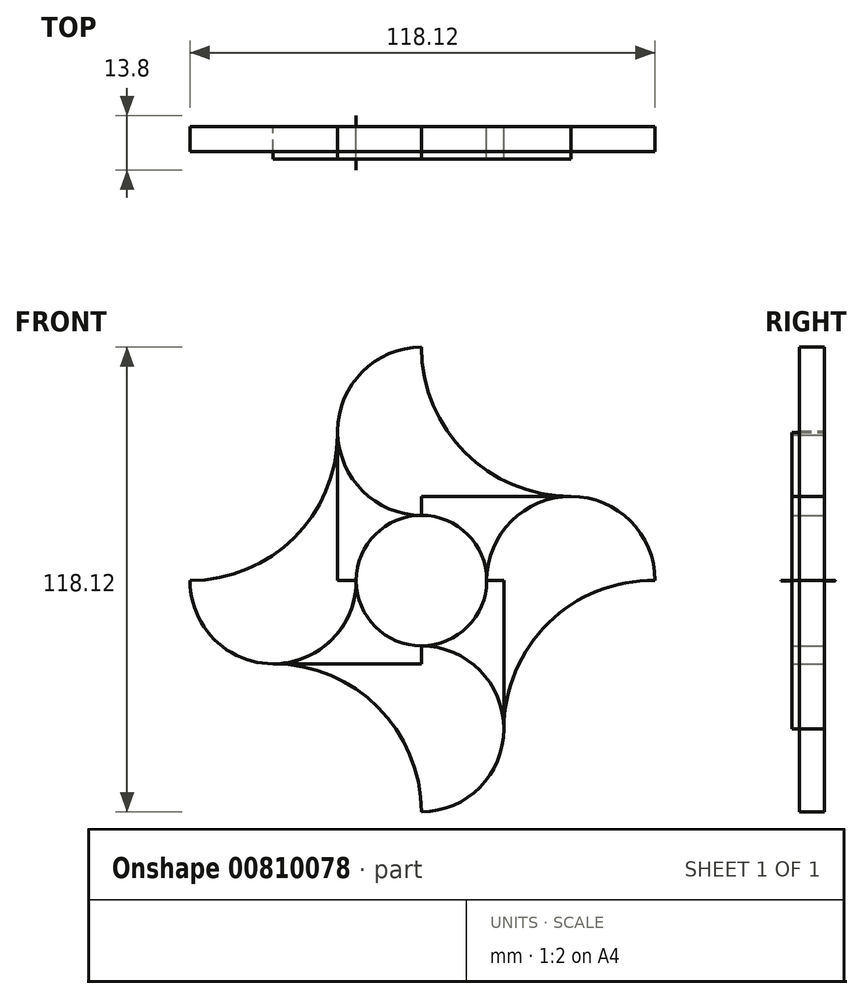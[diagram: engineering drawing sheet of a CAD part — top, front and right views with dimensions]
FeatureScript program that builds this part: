
annotation { "Feature Type Name" : "Feature", "Feature Type Description" : "" }
export const myFeature = defineFeature(function(context is Context, id is Id, definition is map)
    precondition{}
    {
        {
            var Q0;
            Q0=qCreatedBy(makeId("Front.planeOp"),FACE);
            var sketch = newSketch(context, id + "F0", { "sketchPlane" : qUnion([Q0])});
            skCircle(sketch, "E0", {"center": v(0, 0) * mm, "radius": 16.57 * mm});
            skLineSegment(sketch, "E1", {"start": v(0, 16.57) * mm, "end": v(0, 59.34) * mm});
            skPoint(sketch, "E2", {"position": v(0, 37.96) * mm});
            skLineSegment(sketch, "E3", {"start": v(-16.57, 0) * mm, "end": v(-58.78, 0) * mm});
            skPoint(sketch, "E4", {"position": v(-37.68, 0) * mm});
            skLineSegment(sketch, "E5", {"start": v(0, -16.57) * mm, "end": v(0, -58.78) * mm});
            skPoint(sketch, "E6", {"position": v(0, -37.68) * mm});
            skLineSegment(sketch, "E7", {"start": v(16.57, 0) * mm, "end": v(59.34, 0) * mm});
            skPoint(sketch, "E8", {"position": v(37.96, 0) * mm});
            skArc(sketch, "E9", {"start": v(0, 59.34) * mm, "mid": v(-21.28, 37.96) * mm, "end": v(0, 16.57) * mm});
            skArc(sketch, "E10", {"start": v(-58.78, 0) * mm, "mid": v(-37.68, -21.16) * mm, "end": v(-16.57, 0) * mm});
            skArc(sketch, "E11", {"start": v(0, -58.78) * mm, "mid": v(20.93, -37.68) * mm, "end": v(0, -16.57) * mm});
            skArc(sketch, "E12", {"start": v(59.34, 0) * mm, "mid": v(37.96, 21.38) * mm, "end": v(16.57, 0) * mm});
            skPoint(sketch, "E13", {"position": v(-21.28, 37.96) * mm});
            skPoint(sketch, "E14", {"position": v(-37.68, -21.16) * mm});
            skPoint(sketch, "E15", {"position": v(20.93, -37.68) * mm});
            skPoint(sketch, "E16", {"position": v(37.96, 21.38) * mm});
            skPoint(sketch, "E17", {"position": v(0, -21.16) * mm});
            skPoint(sketch, "E18", {"position": v(20.93, 0) * mm});
            skPoint(sketch, "E19", {"position": v(-21.28, 0) * mm});
            skLineSegment(sketch, "E20", {"start": v(-21.28, 37.96) * mm, "end": v(-21.28, 0) * mm});
            skLineSegment(sketch, "E21", {"start": v(-37.68, -21.16) * mm, "end": v(0, -21.16) * mm});
            skLineSegment(sketch, "E22", {"start": v(20.93, -37.68) * mm, "end": v(20.93, 0) * mm});
            skPoint(sketch, "E23", {"position": v(0, 21.38) * mm});
            skLineSegment(sketch, "E24", {"start": v(37.96, 21.38) * mm, "end": v(0, 21.38) * mm});
            skPoint(sketch, "E25", {"position": v(-58.78, 0) * mm});
            skPoint(sketch, "E26", {"position": v(59.34, 0) * mm});
            skPoint(sketch, "E27", {"position": v(0, 59.34) * mm});
            skPoint(sketch, "E28", {"position": v(0, -58.78) * mm});
            skArc(sketch, "E29", {"start": v(0, -58.78) * mm, "mid": v(-11.06, -32.18) * mm, "end": v(-37.68, -21.16) * mm});
            skArc(sketch, "E30", {"start": v(59.34, 0) * mm, "mid": v(32.23, -10.78) * mm, "end": v(20.93, -37.68) * mm});
            skArc(sketch, "E31", {"start": v(0, 59.34) * mm, "mid": v(11.12, 32.5) * mm, "end": v(37.96, 21.38) * mm});
            skArc(sketch, "E32", {"start": v(-58.78, 0) * mm, "mid": v(-32.1, 11.15) * mm, "end": v(-21.28, 37.96) * mm});
            skSolve(sketch);
        }
        {
            var Q0;
            {var subQ5=sQuery(id+"F0.wireOp",EDGE,"E24");Q0=makeQuery(id+"F0.imprint","IMPRINT",FACE,{"disambiguationData":[TD([[makeQuery(id+"F0.imprint","IMPRINT",EDGE,{"derivedFrom":subQ5}),1.0]])]});}
            var Q1;
            {var subQ1=sQuery(id+"F0.wireOp",EDGE,"E3");var subQ5=sQuery(id+"F0.wireOp",EDGE,"E0");var subQ6=makeQuery(id+"F0.imprint","INTERSECT",VERTEX,{"derivedFrom":[subQ5,subQ1]});Q1=makeQuery(id+"F0.imprint","IMPRINT",FACE,{"disambiguationData":[TD([[makeQuery(id+"F0.imprint","IMPRINT",EDGE,{"disambiguationData":[TD([[subQ6,-1.0]])],"derivedFrom":subQ1}),-1.0]])]});}
            var Q2;
            {var subQ5=sQuery(id+"F0.wireOp",EDGE,"E21");Q2=makeQuery(id+"F0.imprint","IMPRINT",FACE,{"disambiguationData":[TD([[makeQuery(id+"F0.imprint","IMPRINT",EDGE,{"derivedFrom":subQ5}),1.0]])]});}
            var Q3;
            {var subQ5=sQuery(id+"F0.wireOp",EDGE,"E22");Q3=makeQuery(id+"F0.imprint","IMPRINT",FACE,{"disambiguationData":[TD([[makeQuery(id+"F0.imprint","IMPRINT",EDGE,{"derivedFrom":subQ5}),1.0]])]});}
            extrude(context, id + "F1", {"entities" : qUnion([Q0, Q1, Q2, Q3]), "depth" : 8.2 * mm, "offsetDistance" : 25 * mm});
        }
        {
            var Q0;
            {var subQ0=sQuery(id+"F0.wireOp",EDGE,"E0");var subQ3=makeQuery(id+"F0.imprint","INTERSECT",VERTEX,{"derivedFrom":[subQ0,sQuery(id+"F0.wireOp",EDGE,"E3")]});Q0=makeQuery(id+"F0.imprint","IMPRINT",FACE,{"disambiguationData":[TD([[makeQuery(id+"F0.imprint","IMPRINT",EDGE,{"disambiguationData":[TD([[subQ3,-1.0]])],"derivedFrom":subQ0}),1.0]])]});}
            extrude(context, id + "F2", {"entities" : qUnion([Q0]), "depth" : 11 * mm, "offsetDistance" : 25 * mm});
        }
        {
            var Q0;
            Q0=makeQuery(id+"F2.opExtrude","CAP_FACE",FACE,{"disambiguationData":[OSD([sQuery(id+"F0.wireOp",EDGE,"E0")])],"isStart":false});
            extrude(context, id + "F3", {"entities" : qUnion([Q0]), "oppositeDirection" : true, "depth" : 13.8 * mm, "offsetDistance" : 25 * mm});
        }
        {
            var Q0;
            {var subQ1=sQuery(id+"F0.wireOp",EDGE,"E1");var subQ7=makeQuery(id+"F0.imprint","INTERSECT",VERTEX,{"derivedFrom":[subQ1,sQuery(id+"F0.wireOp",EDGE,"E24")]});Q0=makeQuery(id+"F0.imprint","IMPRINT",FACE,{"disambiguationData":[TD([[makeQuery(id+"F0.imprint","IMPRINT",EDGE,{"disambiguationData":[TD([[subQ7,1.0]])],"derivedFrom":subQ1}),1.0]])]});}
            var Q1;
            {var subQ2=sQuery(id+"F0.wireOp",EDGE,"E24");Q1=makeQuery(id+"F0.imprint","IMPRINT",FACE,{"disambiguationData":[TD([[makeQuery(id+"F0.imprint","IMPRINT",EDGE,{"derivedFrom":subQ2}),-1.0]])]});}
            var Q2;
            {var subQ1=sQuery(id+"F0.wireOp",EDGE,"E7");var subQ4=makeQuery(id+"F0.imprint","INTERSECT",VERTEX,{"derivedFrom":[subQ1,sQuery(id+"F0.wireOp",EDGE,"E22")]});Q2=makeQuery(id+"F0.imprint","IMPRINT",FACE,{"disambiguationData":[TD([[makeQuery(id+"F0.imprint","IMPRINT",EDGE,{"disambiguationData":[TD([[subQ4,-1.0]])],"derivedFrom":subQ1}),1.0]])]});}
            var Q3;
            {var subQ0=sQuery(id+"F0.wireOp",EDGE,"E22");Q3=makeQuery(id+"F0.imprint","IMPRINT",FACE,{"disambiguationData":[TD([[makeQuery(id+"F0.imprint","IMPRINT",EDGE,{"derivedFrom":subQ0}),-1.0]])]});}
            var Q4;
            {var subQ1=sQuery(id+"F0.wireOp",EDGE,"E5");var subQ3=makeQuery(id+"F0.imprint","INTERSECT",VERTEX,{"derivedFrom":[subQ1,sQuery(id+"F0.wireOp",EDGE,"E21")]});Q4=makeQuery(id+"F0.imprint","IMPRINT",FACE,{"disambiguationData":[TD([[makeQuery(id+"F0.imprint","IMPRINT",EDGE,{"disambiguationData":[TD([[subQ3,1.0]])],"derivedFrom":subQ1}),1.0]])]});}
            var Q5;
            {var subQ2=sQuery(id+"F0.wireOp",EDGE,"E21");Q5=makeQuery(id+"F0.imprint","IMPRINT",FACE,{"disambiguationData":[TD([[makeQuery(id+"F0.imprint","IMPRINT",EDGE,{"derivedFrom":subQ2}),-1.0]])]});}
            var Q6;
            {var subQ1=sQuery(id+"F0.wireOp",EDGE,"E3");var subQ5=sQuery(id+"F0.wireOp",EDGE,"E0");var subQ6=makeQuery(id+"F0.imprint","INTERSECT",VERTEX,{"derivedFrom":[subQ5,subQ1]});Q6=makeQuery(id+"F0.imprint","IMPRINT",FACE,{"disambiguationData":[TD([[makeQuery(id+"F0.imprint","IMPRINT",EDGE,{"disambiguationData":[TD([[subQ6,-1.0]])],"derivedFrom":subQ5}),-1.0]])]});}
            var Q7;
            {var subQ1=sQuery(id+"F0.wireOp",EDGE,"E3");var subQ3=sQuery(id+"F0.wireOp",EDGE,"E20");var subQ4=makeQuery(id+"F0.imprint","INTERSECT",VERTEX,{"derivedFrom":[subQ1,subQ3]});Q7=makeQuery(id+"F0.imprint","IMPRINT",FACE,{"disambiguationData":[TD([[makeQuery(id+"F0.imprint","IMPRINT",EDGE,{"disambiguationData":[TD([[subQ4,1.0]])],"derivedFrom":subQ3}),-1.0]])]});}
            extrude(context, id + "F4", {"entities" : qUnion([Q0, Q1, Q2, Q3, Q4, Q5, Q6, Q7]), "depth" : 6.3 * mm, "offsetDistance" : 25 * mm});
        }
    });
